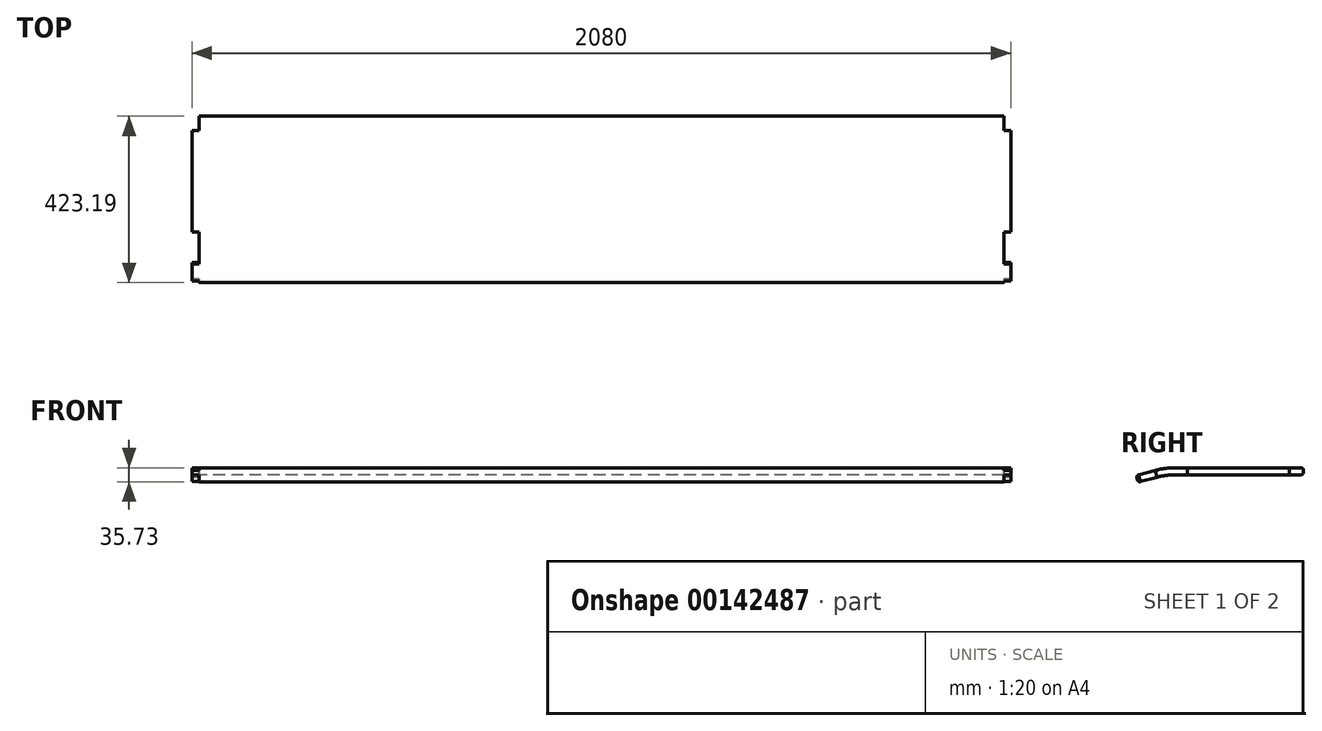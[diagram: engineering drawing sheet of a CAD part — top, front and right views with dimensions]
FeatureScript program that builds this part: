
annotation { "Feature Type Name" : "Feature", "Feature Type Description" : "" }
export const myFeature = defineFeature(function(context is Context, id is Id, definition is map)
    precondition{}
    {
        {
            var Q0;
            Q0=qCreatedBy(makeId("Right.planeOp"),FACE);
            var sketch = newSketch(context, id + "F0", { "sketchPlane" : qUnion([Q0])});
            skLineSegment(sketch, "E0", {"start": v(-6, 0) * mm, "end": v(-325, 0) * mm});
            skLineSegment(sketch, "E1", {"start": v(-371.59, -6.13) * mm, "end": v(-414.09, -17.52) * mm});
            skPoint(sketch, "E2.visualSharp", {"position": v(-348.7, 0) * mm});
            skArc(sketch, "E2.filletArc", {"start": v(-325, 0) * mm, "mid": v(-348.5, -1.54) * mm, "end": v(-371.59, -6.13) * mm});
            skLineSegment(sketch, "E3.0", {"start": v(-376.25, 11.25) * mm, "end": v(-418.75, -0.13) * mm});
            skArc(sketch, "E3.1", {"start": v(-325, 18) * mm, "mid": v(-350.84, 16.3) * mm, "end": v(-376.25, 11.25) * mm});
            skLineSegment(sketch, "E3.2", {"start": v(-6, 18) * mm, "end": v(-325, 18) * mm});
            skLineSegment(sketch, "E4", {"start": v(-422.99, -7.48) * mm, "end": v(-421.44, -13.28) * mm});
            skLineSegment(sketch, "E5", {"start": v(0, 6) * mm, "end": v(0, 12) * mm});
            skPoint(sketch, "E6.visualSharp", {"position": v(-424.54, -1.69) * mm});
            skArc(sketch, "E6.filletArc", {"start": v(-418.75, -0.13) * mm, "mid": v(-422.4, -2.93) * mm, "end": v(-422.99, -7.48) * mm});
            skPoint(sketch, "E7.visualSharp", {"position": v(-419.88, -19.07) * mm});
            skArc(sketch, "E7.filletArc", {"start": v(-421.44, -13.28) * mm, "mid": v(-418.64, -16.92) * mm, "end": v(-414.09, -17.52) * mm});
            skPoint(sketch, "E8.visualSharp", {"position": v(0, 18) * mm});
            skArc(sketch, "E8.filletArc", {"start": v(0, 12) * mm, "mid": v(-1.76, 16.24) * mm, "end": v(-6, 18) * mm});
            skPoint(sketch, "E9.visualSharp", {"position": v(0, 0) * mm});
            skArc(sketch, "E9.filletArc", {"start": v(-6, 0) * mm, "mid": v(-1.76, 1.76) * mm, "end": v(0, 6) * mm});
            skSolve(sketch);
        }
        {
            var Q0;
            Q0=makeQuery(id+"F0.imprint","IMPRINT",FACE,{"disambiguationData":[TD([[makeQuery(id+"F0.imprint","IMPRINT",EDGE,{"derivedFrom":sQuery(id+"F0.wireOp",EDGE,"E0")}),-1.0]])]});
            extrude(context, id + "F1", {"entities" : qUnion([Q0]), "depth" : 2080 * mm});
        }
        {
            var Q0;
            Q0=makeQuery(id+"F1.opExtrude","SWEPT_FACE",FACE,{"disambiguationData":[OSD([sQuery(id+"F0.wireOp",EDGE,"E3.2")])]});
            var sketch = newSketch(context, id + "F2", { "sketchPlane" : qUnion([Q0])});
            skLineSegment(sketch, "E10.0", {"start": v(2062, 15.2) * mm, "end": v(2062, -36) * mm});
            skLineSegment(sketch, "E11.0", {"start": v(2101.97, -36) * mm, "end": v(2062, -36) * mm});
            skLineSegment(sketch, "E12.0", {"start": v(2101.97, -295) * mm, "end": v(2062, -295) * mm});
            skLineSegment(sketch, "E13", {"start": v(-16.22, -361.95) * mm, "end": v(18, -361.95) * mm});
            skLineSegment(sketch, "E14", {"start": v(2062, 15.2) * mm, "end": v(2101.97, 15.2) * mm});
            skLineSegment(sketch, "E15", {"start": v(2101.97, 15.2) * mm, "end": v(2101.97, -36) * mm});
            skLineSegment(sketch, "E16.trimOffspring", {"start": v(2101.97, -295) * mm, "end": v(2101.97, -361.95) * mm});
            skLineSegment(sketch, "E17.trimOffspring", {"start": v(2062, -295) * mm, "end": v(2062, -361.95) * mm});
            skLineSegment(sketch, "E18.0", {"start": v(18, 26.67) * mm, "end": v(18, -36) * mm});
            skLineSegment(sketch, "E19", {"start": v(-16.22, -361.95) * mm, "end": v(-16.22, -295) * mm});
            skLineSegment(sketch, "E20", {"start": v(-16.22, 26.67) * mm, "end": v(18, 26.67) * mm});
            skLineSegment(sketch, "E21.trimOffspring", {"start": v(2062, -361.95) * mm, "end": v(2101.97, -361.95) * mm});
            skLineSegment(sketch, "E22.trimOffspring", {"start": v(18, -295) * mm, "end": v(-16.22, -295) * mm});
            skLineSegment(sketch, "E23.trimOffspring", {"start": v(18, -36) * mm, "end": v(-16.22, -36) * mm});
            skLineSegment(sketch, "E24.trimOffspring", {"start": v(18, -295) * mm, "end": v(18, -361.95) * mm});
            skLineSegment(sketch, "E25.trimOffspring", {"start": v(-16.22, -36) * mm, "end": v(-16.22, 26.67) * mm});
            skSolve(sketch);
        }
        {
            var Q0;
            Q0 = qSketchRegion(id + "F2", true);
            extrude(context, id + "F3", {"entities" : qUnion([Q0]), "operationType" : NewBodyOperationType.REMOVE, "oppositeDirection" : true, "depth" : 25 * mm});
        }
        {
            var Q0;
            Q0=makeQuery(id+"F1.opExtrude","SWEPT_FACE",FACE,{"disambiguationData":[OSD([sQuery(id+"F0.wireOp",EDGE,"E3.0")])]});
            var sketch = newSketch(context, id + "F4", { "sketchPlane" : qUnion([Q0])});
            skLineSegment(sketch, "E26", {"start": v(-19.15, -404.51) * mm, "end": v(18, -404.51) * mm});
            skLineSegment(sketch, "E27", {"start": v(-19.15, -360.51) * mm, "end": v(18, -360.51) * mm});
            skLineSegment(sketch, "E28.0", {"start": v(18, -338.96) * mm, "end": v(18, -418.6) * mm});
            skLineSegment(sketch, "E29.0", {"start": v(2062, -337.03) * mm, "end": v(2062, -360.51) * mm});
            skLineSegment(sketch, "E30", {"start": v(2094.3, -421.42) * mm, "end": v(2094.3, -404.51) * mm});
            skLineSegment(sketch, "E31", {"start": v(-19.15, -418.6) * mm, "end": v(-19.15, -404.51) * mm});
            skLineSegment(sketch, "E32", {"start": v(18, -418.6) * mm, "end": v(-19.15, -418.6) * mm});
            skLineSegment(sketch, "E33", {"start": v(-19.15, -338.96) * mm, "end": v(18, -338.96) * mm});
            skLineSegment(sketch, "E34.trimOffspring", {"start": v(-19.15, -360.51) * mm, "end": v(-19.15, -338.96) * mm});
            skLineSegment(sketch, "E35", {"start": v(2062, -421.42) * mm, "end": v(2094.3, -421.42) * mm});
            skLineSegment(sketch, "E36", {"start": v(2062, -337.03) * mm, "end": v(2094.3, -337.03) * mm});
            skLineSegment(sketch, "E37.trimOffspring", {"start": v(2062, -404.51) * mm, "end": v(2094.3, -404.51) * mm});
            skLineSegment(sketch, "E38.trimOffspring", {"start": v(2062, -360.51) * mm, "end": v(2094.3, -360.51) * mm});
            skLineSegment(sketch, "E39.trimOffspring", {"start": v(2062, -404.51) * mm, "end": v(2062, -421.42) * mm});
            skLineSegment(sketch, "E40.trimOffspring", {"start": v(2094.3, -360.51) * mm, "end": v(2094.3, -337.03) * mm});
            skSolve(sketch);
        }
        {
            var Q0;
            Q0 = qSketchRegion(id + "F4", true);
            extrude(context, id + "F5", {"entities" : qUnion([Q0]), "operationType" : NewBodyOperationType.REMOVE, "oppositeDirection" : true, "depth" : 25 * mm});
        }
    });
